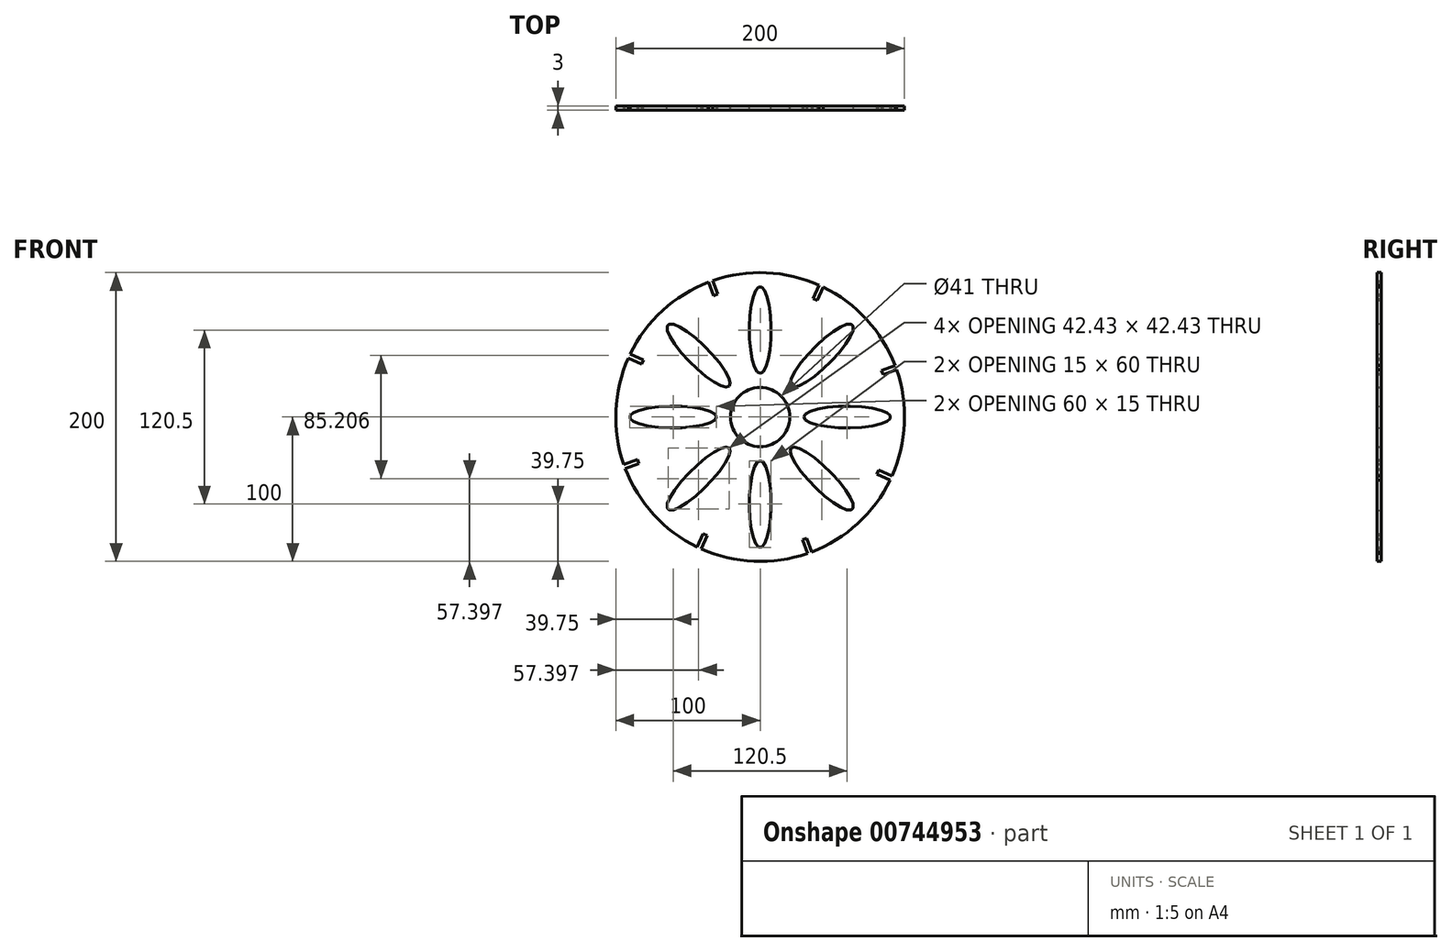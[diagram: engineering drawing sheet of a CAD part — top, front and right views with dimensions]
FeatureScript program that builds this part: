
annotation { "Feature Type Name" : "Feature", "Feature Type Description" : "" }
export const myFeature = defineFeature(function(context is Context, id is Id, definition is map)
    precondition{}
    {
        {
            var Q0;
            Q0=qCreatedBy(makeId("Front.planeOp"),FACE);
            var sketch = newSketch(context, id + "F0", { "sketchPlane" : qUnion([Q0])});
            skCircle(sketch, "E0", {"center": v(0, 0) * mm, "radius": 20.5 * mm});
            skCircle(sketch, "E1", {"center": v(0, 0) * mm, "radius": 100 * mm});
            skEllipse(sketch, "E2", {"center": v(-60.25, 0) * mm, "majorRadius": 30 * mm, "minorRadius": 7.5 * mm, "majorAxis": v(1, 0)});
            skEllipse(sketch, "E3.1.0", {"center": v(-42.6, -42.6) * mm, "majorRadius": 30 * mm, "minorRadius": 7.5 * mm, "majorAxis": v(0.7, 0.7)});
            skEllipse(sketch, "E3.2.0", {"center": v(0, -60.25) * mm, "majorRadius": 30 * mm, "minorRadius": 7.5 * mm, "majorAxis": v(0, 1)});
            skEllipse(sketch, "E3.3.0", {"center": v(42.6, -42.6) * mm, "majorRadius": 30 * mm, "minorRadius": 7.5 * mm, "majorAxis": v(-0.7, 0.7)});
            skEllipse(sketch, "E3.4.0", {"center": v(60.25, 0) * mm, "majorRadius": 30 * mm, "minorRadius": 7.5 * mm, "majorAxis": v(-1, 0)});
            skEllipse(sketch, "E3.5.0", {"center": v(42.6, 42.6) * mm, "majorRadius": 30 * mm, "minorRadius": 7.5 * mm, "majorAxis": v(-0.7, -0.7)});
            skEllipse(sketch, "E3.6.0", {"center": v(0, 60.25) * mm, "majorRadius": 30 * mm, "minorRadius": 7.5 * mm, "majorAxis": v(0, -1)});
            skEllipse(sketch, "E3.7.0", {"center": v(-42.6, 42.6) * mm, "majorRadius": 30 * mm, "minorRadius": 7.5 * mm, "majorAxis": v(0.7, -0.7)});
            skSolve(sketch);
        }
        {
            var Q0;
            Q0 = qSketchRegion(id + "F0", true);
            extrude(context, id + "F1", {"entities" : qUnion([Q0]), "depth" : 3 * mm, "offsetDistance" : 25 * mm});
        }
        {
            var Q0;
            Q0=makeQuery(id+"F1.opExtrude","CAP_FACE",FACE,{"disambiguationData":[OSD([sQuery(id+"F0.wireOp",EDGE,"E0"),sQuery(id+"F0.wireOp",EDGE,"E1"),sQuery(id+"F0.wireOp",EDGE,"E2"),sQuery(id+"F0.wireOp",EDGE,"E3.1.0"),sQuery(id+"F0.wireOp",EDGE,"E3.2.0"),sQuery(id+"F0.wireOp",EDGE,"E3.3.0"),sQuery(id+"F0.wireOp",EDGE,"E3.4.0"),sQuery(id+"F0.wireOp",EDGE,"E3.5.0"),sQuery(id+"F0.wireOp",EDGE,"E3.6.0"),sQuery(id+"F0.wireOp",EDGE,"E3.7.0")])],"isStart":true});
            var sketch = newSketch(context, id + "F2", { "sketchPlane" : qUnion([Q0])});
            skLineSegment(sketch, "E4", {"start": v(0, 0) * mm, "end": v(-90.21, 0) * mm, "construction": true});
            skLineSegment(sketch, "E5", {"start": v(0, 0) * mm, "end": v(-81.57, -38.04) * mm, "construction": true});
            skLineSegment(sketch, "E6.bottom", {"start": v(-100.33, -45.13) * mm, "end": v(-82.2, -36.68) * mm});
            skLineSegment(sketch, "E6.top", {"start": v(-99.06, -47.85) * mm, "end": v(-80.93, -39.4) * mm});
            skLineSegment(sketch, "E6.left", {"start": v(-100.33, -45.13) * mm, "end": v(-99.06, -47.85) * mm});
            skLineSegment(sketch, "E6.right", {"start": v(-82.2, -36.68) * mm, "end": v(-80.93, -39.4) * mm});
            skLineSegment(sketch, "E7.1.0", {"start": v(-32.2, -84.06) * mm, "end": v(-29.37, -85.09) * mm});
            skLineSegment(sketch, "E7.1.1", {"start": v(-39.03, -102.85) * mm, "end": v(-36.21, -103.88) * mm});
            skLineSegment(sketch, "E7.1.2", {"start": v(-36.21, -103.88) * mm, "end": v(-29.37, -85.09) * mm});
            skLineSegment(sketch, "E7.1.3", {"start": v(-39.03, -102.85) * mm, "end": v(-32.2, -84.06) * mm});
            skLineSegment(sketch, "E7.2.0", {"start": v(36.68, -82.2) * mm, "end": v(39.4, -80.93) * mm});
            skLineSegment(sketch, "E7.2.1", {"start": v(45.13, -100.33) * mm, "end": v(47.85, -99.06) * mm});
            skLineSegment(sketch, "E7.2.2", {"start": v(47.85, -99.06) * mm, "end": v(39.4, -80.93) * mm});
            skLineSegment(sketch, "E7.2.3", {"start": v(45.13, -100.33) * mm, "end": v(36.68, -82.2) * mm});
            skPoint(sketch, "E7.center", {"position": v(0, 0) * mm});
            skLineSegment(sketch, "E8.3.3.0", {"start": v(102.85, -39.03) * mm, "end": v(103.88, -36.21) * mm});
            skLineSegment(sketch, "E8.5.3.0", {"start": v(84.06, -32.2) * mm, "end": v(85.09, -29.37) * mm});
            skLineSegment(sketch, "E8.6.3.0", {"start": v(103.88, -36.21) * mm, "end": v(85.09, -29.37) * mm});
            skLineSegment(sketch, "E8.9.3.0", {"start": v(102.85, -39.03) * mm, "end": v(84.06, -32.2) * mm});
            skLineSegment(sketch, "E8.3.4.0", {"start": v(100.33, 45.13) * mm, "end": v(99.06, 47.85) * mm});
            skLineSegment(sketch, "E8.5.4.0", {"start": v(82.2, 36.68) * mm, "end": v(80.93, 39.4) * mm});
            skLineSegment(sketch, "E8.6.4.0", {"start": v(99.06, 47.85) * mm, "end": v(80.93, 39.4) * mm});
            skLineSegment(sketch, "E8.9.4.0", {"start": v(100.33, 45.13) * mm, "end": v(82.2, 36.68) * mm});
            skLineSegment(sketch, "E8.3.5.0", {"start": v(39.03, 102.85) * mm, "end": v(36.21, 103.88) * mm});
            skLineSegment(sketch, "E8.5.5.0", {"start": v(32.2, 84.06) * mm, "end": v(29.37, 85.09) * mm});
            skLineSegment(sketch, "E8.6.5.0", {"start": v(36.21, 103.88) * mm, "end": v(29.37, 85.09) * mm});
            skLineSegment(sketch, "E8.9.5.0", {"start": v(39.03, 102.85) * mm, "end": v(32.2, 84.06) * mm});
            skLineSegment(sketch, "E8.3.6.0", {"start": v(-45.13, 100.33) * mm, "end": v(-47.85, 99.06) * mm});
            skLineSegment(sketch, "E8.5.6.0", {"start": v(-36.68, 82.2) * mm, "end": v(-39.4, 80.93) * mm});
            skLineSegment(sketch, "E8.6.6.0", {"start": v(-47.85, 99.06) * mm, "end": v(-39.4, 80.93) * mm});
            skLineSegment(sketch, "E8.9.6.0", {"start": v(-45.13, 100.33) * mm, "end": v(-36.68, 82.2) * mm});
            skLineSegment(sketch, "E8.3.7.0", {"start": v(-102.85, 39.03) * mm, "end": v(-103.88, 36.21) * mm});
            skLineSegment(sketch, "E8.5.7.0", {"start": v(-84.06, 32.2) * mm, "end": v(-85.09, 29.37) * mm});
            skLineSegment(sketch, "E8.6.7.0", {"start": v(-103.88, 36.21) * mm, "end": v(-85.09, 29.37) * mm});
            skLineSegment(sketch, "E8.9.7.0", {"start": v(-102.85, 39.03) * mm, "end": v(-84.06, 32.2) * mm});
            skSolve(sketch);
        }
        {
            var Q0;
            Q0 = qSketchRegion(id + "F2", true);
            extrude(context, id + "F3", {"entities" : qUnion([Q0]), "operationType" : NewBodyOperationType.REMOVE, "oppositeDirection" : true, "depth" : 3 * mm, "offsetDistance" : 25 * mm});
        }
    });
